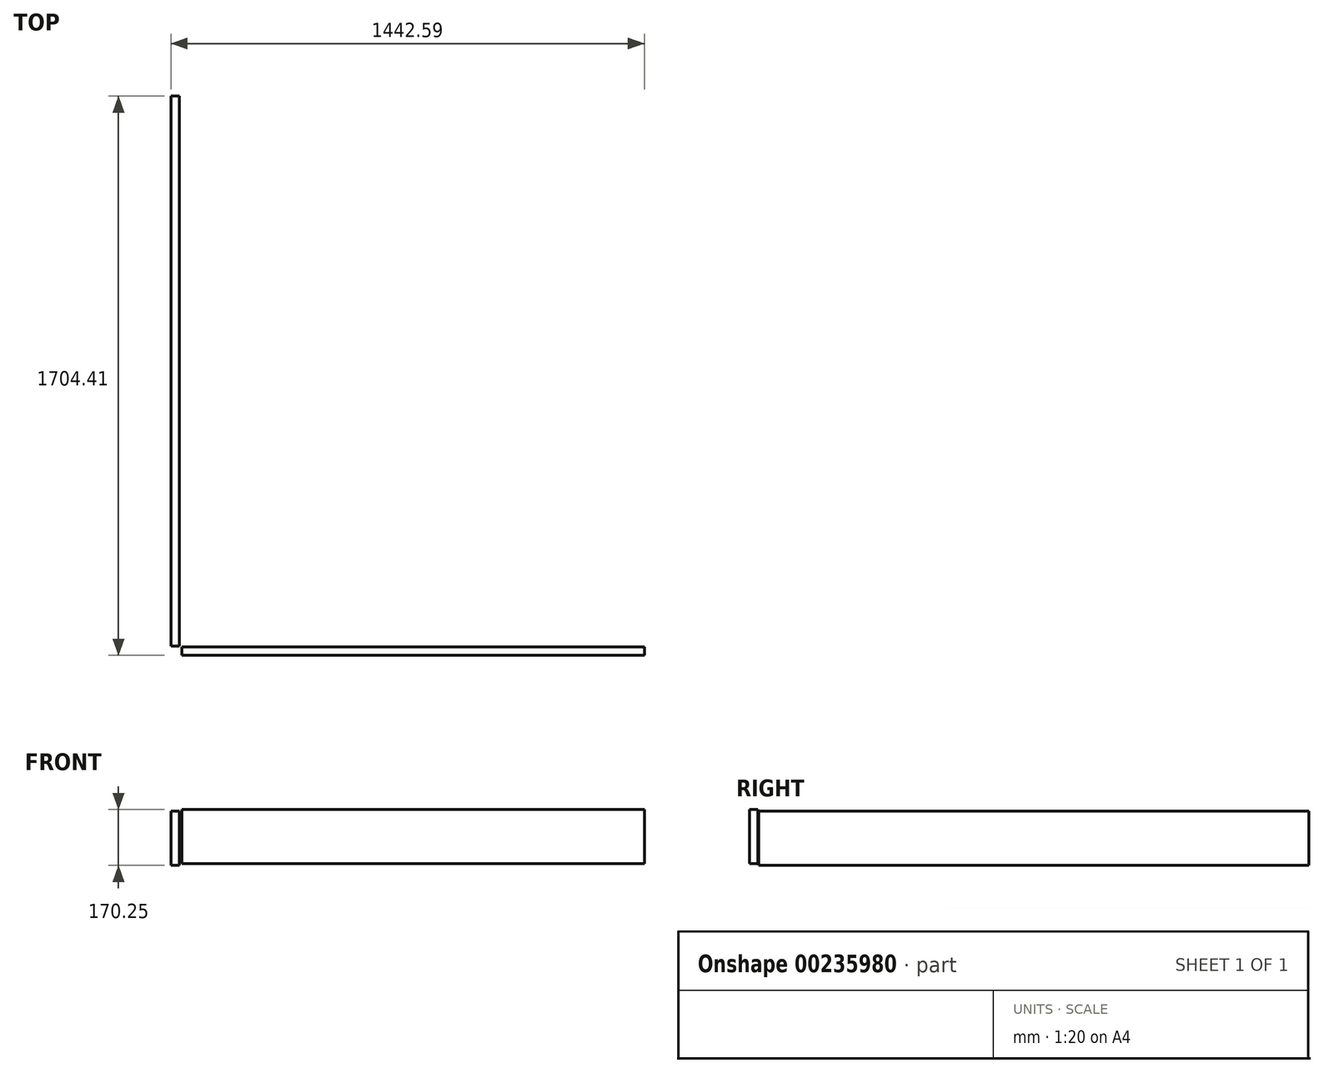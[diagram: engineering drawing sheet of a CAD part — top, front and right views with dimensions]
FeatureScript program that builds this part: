
annotation { "Feature Type Name" : "Feature", "Feature Type Description" : "" }
export const myFeature = defineFeature(function(context is Context, id is Id, definition is map)
    precondition{}
    {
        {
            var Q0;
            Q0=qCreatedBy(makeId("Right.planeOp"),FACE);
            var sketch = newSketch(context, id + "F0", { "sketchPlane" : qUnion([Q0])});
            skLineSegment(sketch, "E0.bottom", {"start": v(2.6, 4.17) * mm, "end": v(1679, 4.17) * mm});
            skLineSegment(sketch, "E0.top", {"start": v(2.6, 169.27) * mm, "end": v(1679, 169.27) * mm});
            skLineSegment(sketch, "E0.left", {"start": v(2.6, 4.17) * mm, "end": v(2.6, 169.27) * mm});
            skLineSegment(sketch, "E0.right", {"start": v(1679, 4.17) * mm, "end": v(1679, 169.27) * mm});
            skSolve(sketch);
        }
        {
            var Q0;
            Q0 = qSketchRegion(id + "F0", true);
            extrude(context, id + "F1", {"entities" : qUnion([Q0]), "depth" : 25.4 * mm});
        }
        {
            var Q0;
            Q0=qCreatedBy(makeId("Front.planeOp"),FACE);
            var sketch = newSketch(context, id + "F2", { "sketchPlane" : qUnion([Q0])});
            skLineSegment(sketch, "E1.bottom", {"start": v(32.9, 9.32) * mm, "end": v(1442.6, 9.32) * mm});
            skLineSegment(sketch, "E1.top", {"start": v(32.9, 174.42) * mm, "end": v(1442.6, 174.42) * mm});
            skLineSegment(sketch, "E1.left", {"start": v(32.9, 9.32) * mm, "end": v(32.9, 174.42) * mm});
            skLineSegment(sketch, "E1.right", {"start": v(1442.6, 9.32) * mm, "end": v(1442.6, 174.42) * mm});
            skSolve(sketch);
        }
        {
            var Q0;
            Q0 = qSketchRegion(id + "F2", true);
            extrude(context, id + "F3", {"entities" : qUnion([Q0]), "depth" : 25.4 * mm});
        }
    });
